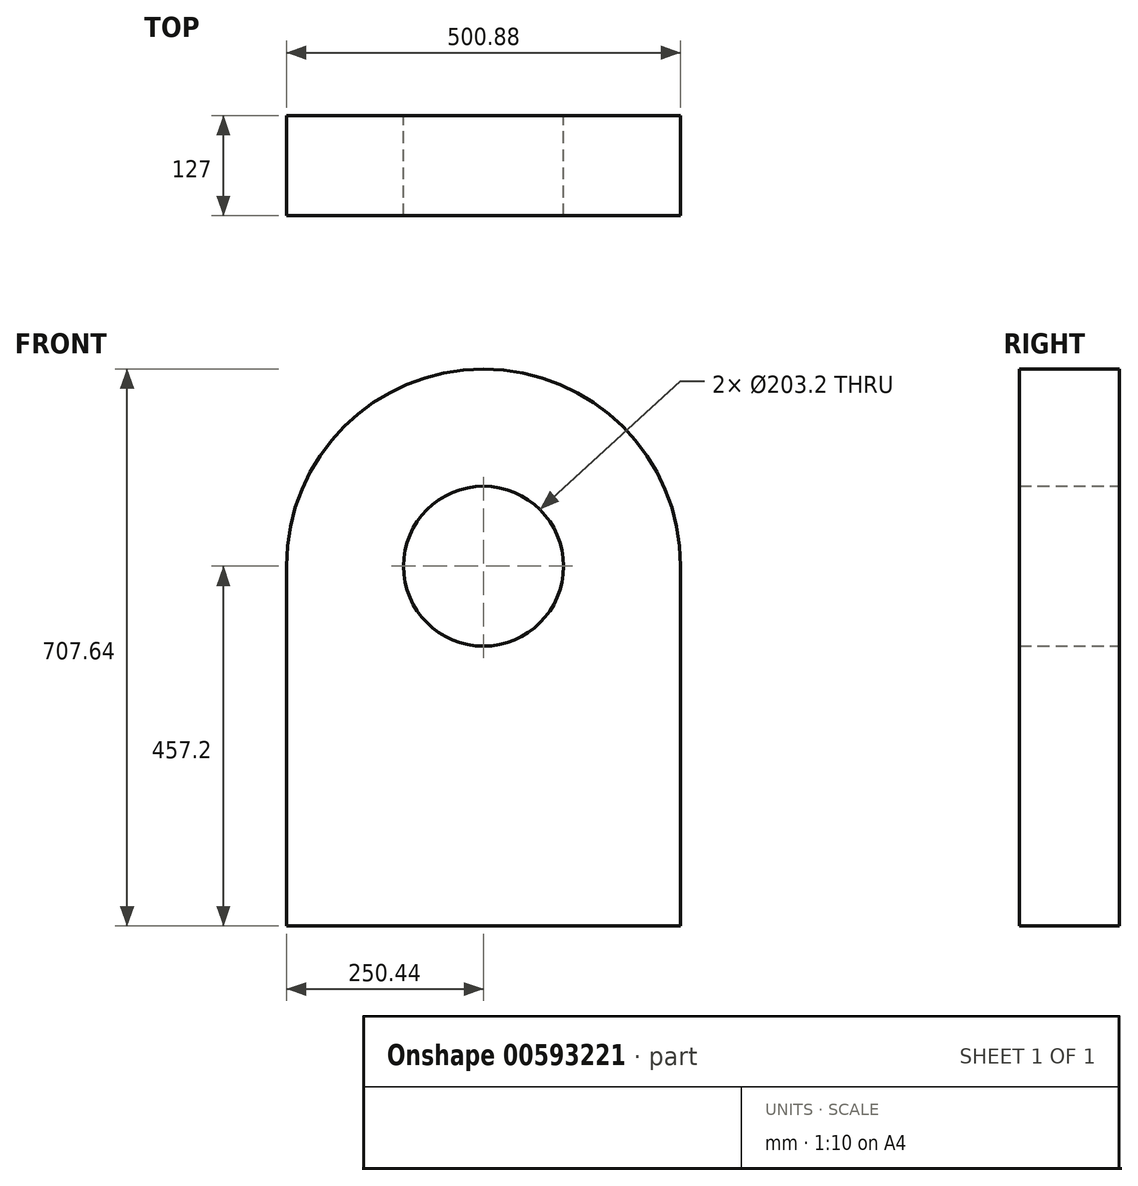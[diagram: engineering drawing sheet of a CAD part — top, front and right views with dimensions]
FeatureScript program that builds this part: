
annotation { "Feature Type Name" : "Feature", "Feature Type Description" : "" }
export const myFeature = defineFeature(function(context is Context, id is Id, definition is map)
    precondition{}
    {
        {
            var Q0;
            Q0=qCreatedBy(makeId("Front.planeOp"),FACE);
            var sketch = newSketch(context, id + "F0", { "sketchPlane" : qUnion([Q0])});
            skLineSegment(sketch, "E0.bottom", {"start": v(-250.44, 457.2) * mm, "end": v(250.44, 457.2) * mm});
            skLineSegment(sketch, "E0.top", {"start": v(-250.44, 0) * mm, "end": v(250.44, 0) * mm});
            skLineSegment(sketch, "E0.left", {"start": v(-250.44, 457.2) * mm, "end": v(-250.44, 0) * mm});
            skLineSegment(sketch, "E0.right", {"start": v(250.44, 457.2) * mm, "end": v(250.44, 0) * mm});
            skCircle(sketch, "E1", {"center": v(0, 457.2) * mm, "radius": 250.44 * mm});
            skCircle(sketch, "E2", {"center": v(0, 457.2) * mm, "radius": 101.6 * mm});
            skSolve(sketch);
        }
        {
            var Q0;
            {var subQ0=sQuery(id+"F0.wireOp",EDGE,"E0.bottom");Q0=makeQuery(id+"F0.imprint","IMPRINT",FACE,{"disambiguationData":[TD([[makeQuery(id+"F0.imprint","IMPRINT",EDGE,{"derivedFrom":subQ0}),-1.0]])]});}
            var Q1;
            {var subQ0=sQuery(id+"F0.wireOp",EDGE,"E0.bottom");Q1=makeQuery(id+"F0.imprint","IMPRINT",FACE,{"disambiguationData":[TD([[makeQuery(id+"F0.imprint","IMPRINT",EDGE,{"derivedFrom":subQ0}),1.0]])]});}
            var Q2;
            Q2=makeQuery(id+"F0.imprint","IMPRINT",FACE,{"disambiguationData":[TD([[makeQuery(id+"F0.imprint","IMPRINT",EDGE,{"derivedFrom":sQuery(id+"F0.wireOp",EDGE,"E0.top")}),1.0]])]});
            extrude(context, id + "F1", {"entities" : qUnion([Q0, Q1, Q2]), "depth" : 127 * mm, "offsetDistance" : 25.4 * mm});
        }
    });
